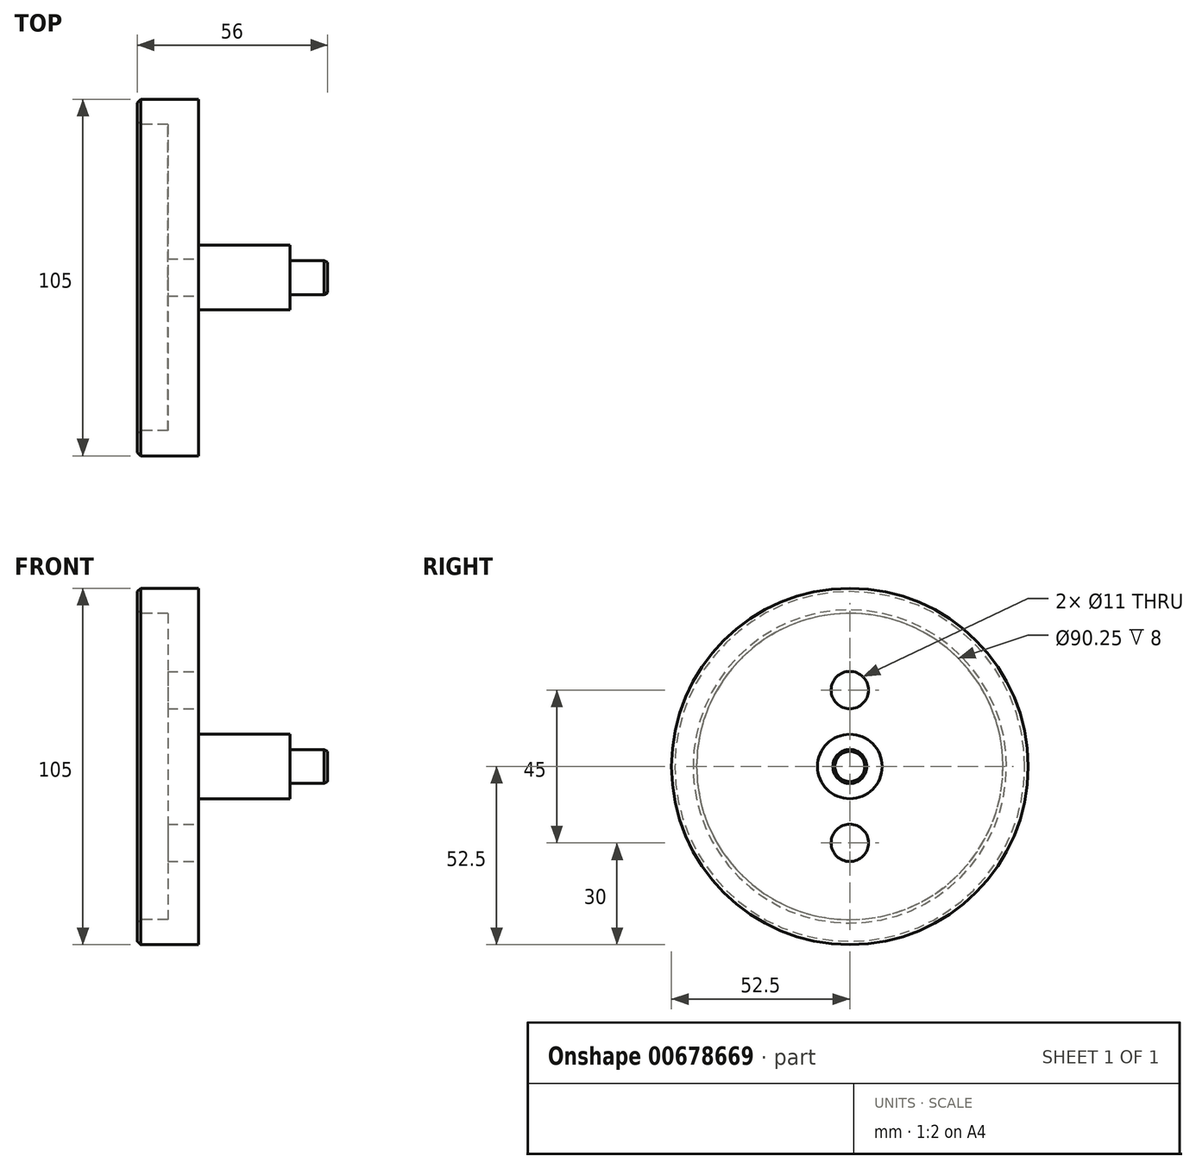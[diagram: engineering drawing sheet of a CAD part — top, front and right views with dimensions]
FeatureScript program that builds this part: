
annotation { "Feature Type Name" : "Feature", "Feature Type Description" : "" }
export const myFeature = defineFeature(function(context is Context, id is Id, definition is map)
    precondition{}
    {
        {
            var Q0;
            Q0=qCreatedBy(makeId("Right.planeOp"),FACE);
            var sketch = newSketch(context, id + "F0", { "sketchPlane" : qUnion([Q0])});
            skCircle(sketch, "E0", {"center": v(0, 0) * mm, "radius": 52.5 * mm});
            skSolve(sketch);
        }
        {
            var Q0;
            Q0 = qSketchRegion(id + "F0", true);
            extrude(context, id + "F1", {"entities" : qUnion([Q0]), "oppositeDirection" : true, "depth" : (56 - 38) * mm, "offsetDistance" : 25 * mm});
        }
        {
            var Q0;
            Q0=makeQuery(id+"F1.opExtrude","CAP_FACE",FACE,{"disambiguationData":[OSD([sQuery(id+"F0.wireOp",EDGE,"E0")])],"isStart":false});
            var sketch = newSketch(context, id + "F2", { "sketchPlane" : qUnion([Q0])});
            skCircle(sketch, "E1", {"center": v(0, 0) * mm, "radius": 45.12 * mm});
            skSolve(sketch);
        }
        {
            var Q0;
            Q0 = qSketchRegion(id + "F2", true);
            extrude(context, id + "F3", {"entities" : qUnion([Q0]), "operationType" : NewBodyOperationType.REMOVE, "oppositeDirection" : true, "depth" : 9 * mm, "offsetDistance" : 25 * mm});
        }
        {
            var Q0;
            Q0=makeQuery(id+"F1.opExtrude","CAP_FACE",FACE,{"disambiguationData":[OSD([sQuery(id+"F0.wireOp",EDGE,"E0")])],"isStart":false});
            chamfer(context, id + "F4", {"entities" : qUnion([Q0]), "width" : 1 * mm, "tangentPropagation" : true});
        }
        {
            var Q0;
            Q0=makeQuery(id+"F1.opExtrude","CAP_FACE",FACE,{"disambiguationData":[OSD([sQuery(id+"F0.wireOp",EDGE,"E0")])],"isStart":true});
            var sketch = newSketch(context, id + "F5", { "sketchPlane" : qUnion([Q0])});
            skCircle(sketch, "E2", {"center": v(0, 0) * mm, "radius": 9.5 * mm});
            skSolve(sketch);
        }
        {
            var Q0;
            Q0 = qSketchRegion(id + "F5", true);
            extrude(context, id + "F6", {"entities" : qUnion([Q0]), "operationType" : NewBodyOperationType.ADD, "depth" : (38 - 11) * mm, "offsetDistance" : 25 * mm});
        }
        {
            var Q0;
            Q0=makeQuery(id+"F6.opExtrude","CAP_FACE",FACE,{"disambiguationData":[OSD([sQuery(id+"F5.wireOp",EDGE,"E2")])],"isStart":false});
            var sketch = newSketch(context, id + "F7", { "sketchPlane" : qUnion([Q0])});
            skCircle(sketch, "E3", {"center": v(0, 0) * mm, "radius": 5 * mm});
            skSolve(sketch);
        }
        {
            var Q0;
            Q0 = qSketchRegion(id + "F7", true);
            extrude(context, id + "F8", {"entities" : qUnion([Q0]), "operationType" : NewBodyOperationType.ADD, "depth" : 11 * mm, "offsetDistance" : 25 * mm});
        }
        {
            var Q0;
            Q0=makeQuery(id+"F8.opExtrude","CAP_EDGE",EDGE,{"disambiguationData":[OSD([sQuery(id+"F7.wireOp",EDGE,"E3")])],"isStart":false});
            chamfer(context, id + "F9", {"entities" : qUnion([Q0]), "chamferType" : ChamferType.OFFSET_ANGLE, "width" : 1 * mm, "oppositeDirection" : true, "angle" : 30 * degree, "tangentPropagation" : true});
        }
        {
            var Q0;
            Q0=makeQuery(id+"F1.opExtrude","CAP_FACE",FACE,{"disambiguationData":[OSD([sQuery(id+"F0.wireOp",EDGE,"E0")])],"isStart":true});
            var sketch = newSketch(context, id + "F10", { "sketchPlane" : qUnion([Q0])});
            skLineSegment(sketch, "E4", {"start": v(0, -22.5) * mm, "end": v(0, 22.5) * mm, "construction": true});
            skPoint(sketch, "E5", {"position": v(0, -22.5) * mm});
            skPoint(sketch, "E6", {"position": v(0, 22.5) * mm});
            skSolve(sketch);
        }
        {
            var Q0;
            Q0=sQuery(id+"F10.wireOp",VERTEX,"E5");
            var Q1;
            Q1=sQuery(id+"F10.wireOp",VERTEX,"E6");
            var Q2;
            Q2=makeQuery(id+"F1.opExtrude","SWEPT_BODY",BODY,{"disambiguationData":[OSD([sQuery(id+"F0.wireOp",EDGE,"E0")])]});
            hole(context, id + "F11", {"style" : HoleStyle.SIMPLE, "endStyle" : HoleEndStyle.THROUGH, "holeDiameter" : 11 * mm, "majorDiameter" : 5 * mm, "isTappedThrough" : true, "tappedDepth" : 24.75 * mm, "tapClearance" : 3, "locations" : qUnion([Q0, Q1]), "scope" : qUnion([Q2])});
        }
    });
